# Revit family: ME_polyethylene cable pit_ACO
name_source: partatom
category: Mechanical Equipment
units: mm (PartAtom-declared; Revit-internal decimal feet)

## family parameters
Always vertical = Yes
Classification = None
Cut with Voids When Loaded = No
OmniClass Number = 23.30.10.27.27
OmniClass Title = Security Hatches
Part Type = Normal
Room Calculation Point = Yes
Round Connector Dimension = Use Diameter
Shared = Yes
Work Plane-Based = No

## types (14) — shared parameters
Description = Cablemate
IfcDescription = Cablemate
IfcExportAs = UserDefined
IfcExportType = Gridtype
Manufacturer = ACO
Model = ACO Polyethylene Pit with lids and riser assembly
Telephone = 1300 765 226
Type Comments = Polyethylene pits have excellent insulation properties, high mechanical strengths, chemical resistance and zero water absorption, which makes them ideal as electrical and communications enclosures.
URL = www.acocablemate.com.au
cement_lid_blank = PE_lids_assembly : cement concrete lid - Blank
cement_lid_comunication = PE_lids_assembly : cement concrete lid - Communications
cement_lid_electricity = PE_lids_assembly : cement concrete lid - Electricity
content_date_changed_C_ANZRS = 25-08-2023
content_version_C_ANZRS = 1.0
info_commercial_C_ANZRS = https://www.acocablemate.com.au
info_technical_C_ANZRS = https://www.acocablemate.com.au
installation_manual = https://www.acocablemate.com.au
instructions_for_use = https://www.acocablemate.com.au
intended_use_C_ANZRS = Electricity and communications
lookup_table_name = cable_pit
material_C_ANZRS = Polyethylene PE
polymer_lid_blank = PE_lids_assembly : polymer concrete lid - Blank
polymer_lid_comunication = PE_lids_assembly : polymer concrete lid - Electricity
polymer_lid_electricity = PE_lids_assembly : polymer concrete lid - Communications
powerlok_lid = PE_lids_assembly : steel powerlok lid
product_assortment_C_ANZRS = Cablemate
region_index = 1
steel_lid = PE_lids_assembly : steel lid
zero-valued in all types: Default Elevation

## per-type parameters (varying)
| type | type_index |
| Type 1 | 1 |
| Type 2 | 2 |
| Type 3 | 3 |
| Type 4 | 4 |
| Type 5 retroribs full | 50 |
| Type 6 | 6 |
| Type 7 | 7 |
| Type 8 retroribs side | 8 |
| Type 8 retroribs full | 80 |
| Type 5 retroribs side | 5 |
| Type 43 | 43 |
| Type 53 | 53 |
| Type 55 | 55 |
| Type 77 | 77 |

## geometry (parser evidence)
native form markers: Sweep x32
no freeform markers — native parametric forms only
